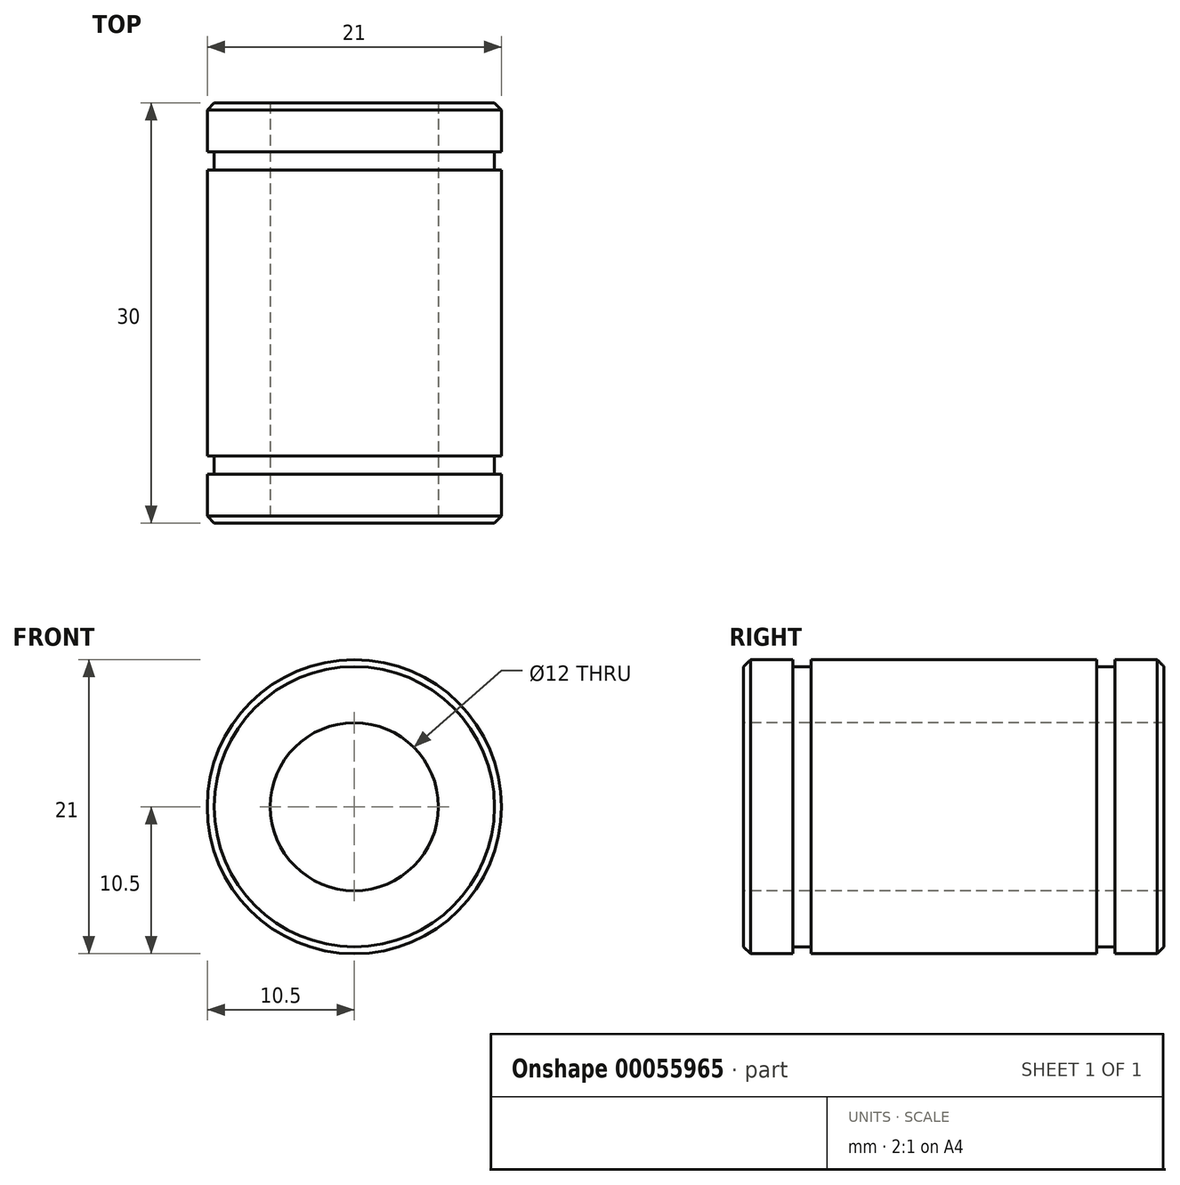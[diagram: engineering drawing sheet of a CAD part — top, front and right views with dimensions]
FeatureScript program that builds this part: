
annotation { "Feature Type Name" : "Feature", "Feature Type Description" : "" }
export const myFeature = defineFeature(function(context is Context, id is Id, definition is map)
    precondition{}
    {
        {
            var Q0;
            Q0=qCreatedBy(makeId("Front.planeOp"),FACE);
            var sketch = newSketch(context, id + "F0", { "sketchPlane" : qUnion([Q0])});
            skCircle(sketch, "E0", {"center": v(0, 0) * mm, "radius": 6 * mm});
            skSolve(sketch);
        }
        {
            var Q0;
            Q0=qCreatedBy(makeId("Right.planeOp"),FACE);
            var sketch = newSketch(context, id + "F1", { "sketchPlane" : qUnion([Q0])});
            skLineSegment(sketch, "E1.0", {"start": v(0, -6) * mm, "end": v(0, 6) * mm});
            skLineSegment(sketch, "E2.bottom", {"start": v(0, 6) * mm, "end": v(30, 6) * mm});
            skLineSegment(sketch, "E2.top", {"start": v(0, 10.5) * mm, "end": v(30, 10.5) * mm});
            skLineSegment(sketch, "E2.left", {"start": v(0, 6) * mm, "end": v(0, 10.5) * mm});
            skLineSegment(sketch, "E2.right", {"start": v(30, 6) * mm, "end": v(30, 10.5) * mm});
            skLineSegment(sketch, "E3", {"start": v(15, 10.5) * mm, "end": v(26.5, 10.5) * mm});
            skLineSegment(sketch, "E4", {"start": v(15, 10.5) * mm, "end": v(3.5, 10.5) * mm});
            skLineSegment(sketch, "E5.bottom", {"start": v(3.5, 10.5) * mm, "end": v(4.8, 10.5) * mm});
            skLineSegment(sketch, "E5.top", {"start": v(3.5, 10) * mm, "end": v(4.8, 10) * mm});
            skLineSegment(sketch, "E5.left", {"start": v(3.5, 10.5) * mm, "end": v(3.5, 10) * mm});
            skLineSegment(sketch, "E5.right", {"start": v(4.8, 10.5) * mm, "end": v(4.8, 10) * mm});
            skLineSegment(sketch, "E6.bottom", {"start": v(26.5, 10.5) * mm, "end": v(25.2, 10.5) * mm});
            skLineSegment(sketch, "E6.top", {"start": v(26.5, 10) * mm, "end": v(25.2, 10) * mm});
            skLineSegment(sketch, "E6.left", {"start": v(26.5, 10.5) * mm, "end": v(26.5, 10) * mm});
            skLineSegment(sketch, "E6.right", {"start": v(25.2, 10.5) * mm, "end": v(25.2, 10) * mm});
            skLineSegment(sketch, "E7.bottom", {"start": v(0, 10.5) * mm, "end": v(0.5, 10.5) * mm});
            skLineSegment(sketch, "E7.left", {"start": v(0, 10.5) * mm, "end": v(0, 10) * mm});
            skLineSegment(sketch, "E8.bottom", {"start": v(30, 10.5) * mm, "end": v(29.5, 10.5) * mm});
            skLineSegment(sketch, "E8.left", {"start": v(30, 10.5) * mm, "end": v(30, 10) * mm});
            skLineSegment(sketch, "E9", {"start": v(0, 10) * mm, "end": v(0.5, 10.5) * mm});
            skLineSegment(sketch, "E10", {"start": v(29.5, 10.5) * mm, "end": v(30, 10) * mm});
            skSolve(sketch);
        }
        {
            var Q0;
            Q0=makeQuery(id+"F1.imprint","IMPRINT",FACE,{"disambiguationData":[TD([[makeQuery(id+"F1.imprint","IMPRINT",EDGE,{"derivedFrom":sQuery(id+"F1.wireOp",EDGE,"E2.bottom")}),1.0]])]});
            var Q1;
            Q1=sQuery(id+"F0.wireOp",EDGE,"E0");
            sweep(context, id + "F2", {"profiles" : qUnion([Q0]), "path" : qUnion([Q1])});
        }
    });
